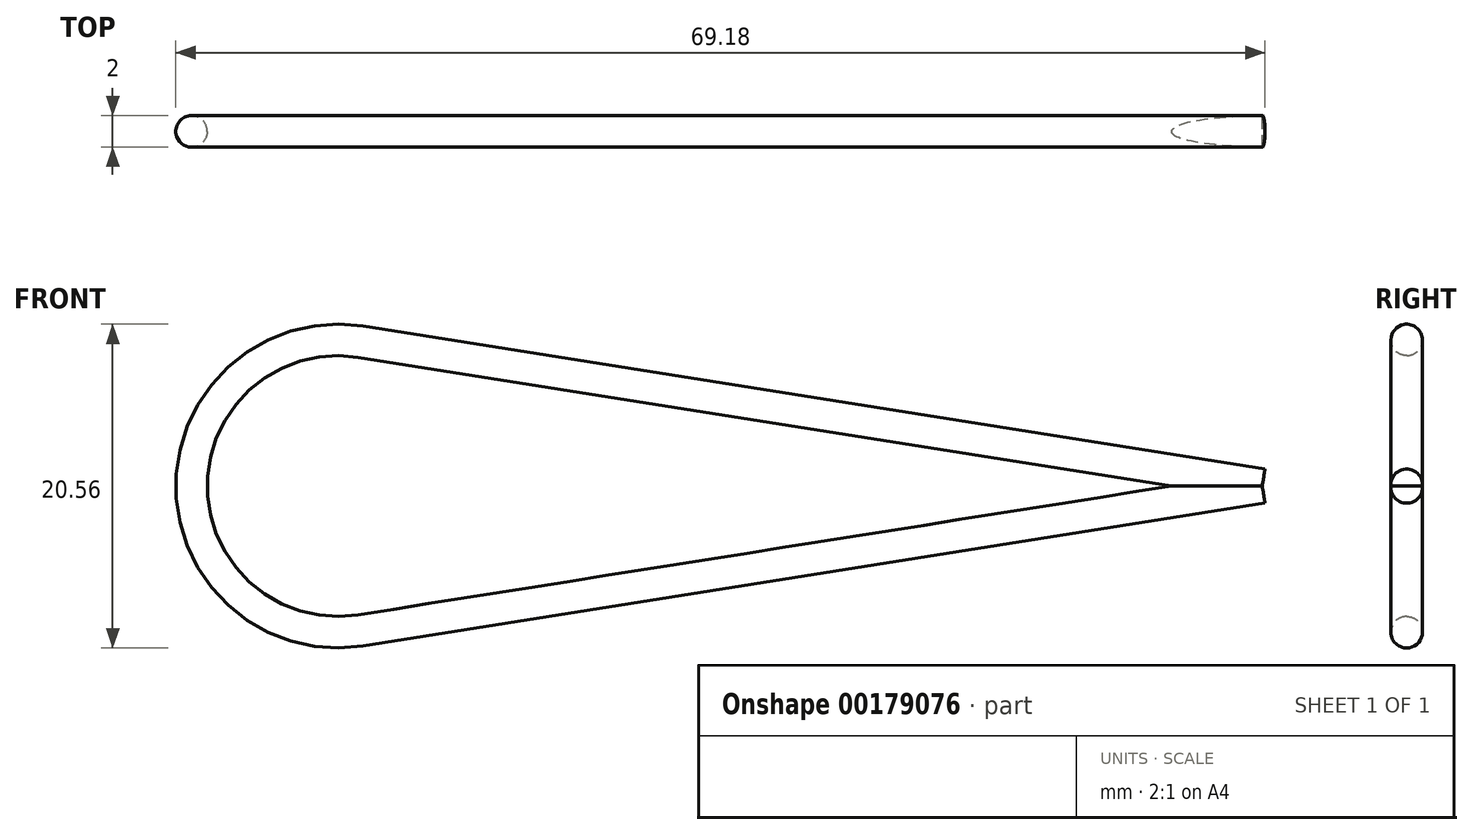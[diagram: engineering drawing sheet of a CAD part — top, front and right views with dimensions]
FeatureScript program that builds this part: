
annotation { "Feature Type Name" : "Feature", "Feature Type Description" : "" }
export const myFeature = defineFeature(function(context is Context, id is Id, definition is map)
    precondition{}
    {
        {
            var Q0;
            Q0=qCreatedBy(makeId("Top.planeOp"),FACE);
            var sketch = newSketch(context, id + "F0", { "sketchPlane" : qUnion([Q0])});
            skCircle(sketch, "E0", {"center": v(0, 0) * mm, "radius": 1 * mm});
            skLineSegment(sketch, "E1", {"start": v(9.28, -3.57) * mm, "end": v(9.28, 4.93) * mm});
            skSolve(sketch);
        }
        {
            var Q0;
            Q0=makeQuery(id+"F0.imprint","IMPRINT",FACE,{"disambiguationData":[TD([[makeQuery(id+"F0.imprint","IMPRINT",EDGE,{"derivedFrom":sQuery(id+"F0.wireOp",EDGE,"E0")}),1.0]])]});
            var Q1;
            Q1=sQuery(id+"F0.wireOp",EDGE,"E1");
            revolve(context, id + "F1", {"entities" : qUnion([Q0]), "axis" : qUnion([Q1]), "revolveType" : RevolveType.TWO_DIRECTIONS, "angle" : 99 * degree, "angleBack" : 261 * degree});
        }
        {
            var Q0;
            Q0=makeQuery(id+"F1.opRevolve","CAP_FACE",FACE,{"disambiguationData":[OSD([sQuery(id+"F0.wireOp",EDGE,"E0")])],"isStart":false});
            extrude(context, id + "F2", {"entities" : qUnion([Q0]), "operationType" : NewBodyOperationType.ADD, "depth" : 58 * mm});
        }
        {
            var Q0;
            Q0=makeQuery(id+"F1.opRevolve","CAP_FACE",FACE,{"disambiguationData":[OSD([sQuery(id+"F0.wireOp",EDGE,"E0")])],"isStart":true});
            extrude(context, id + "F3", {"entities" : qUnion([Q0]), "operationType" : NewBodyOperationType.ADD, "depth" : 58 * mm});
        }
    });
